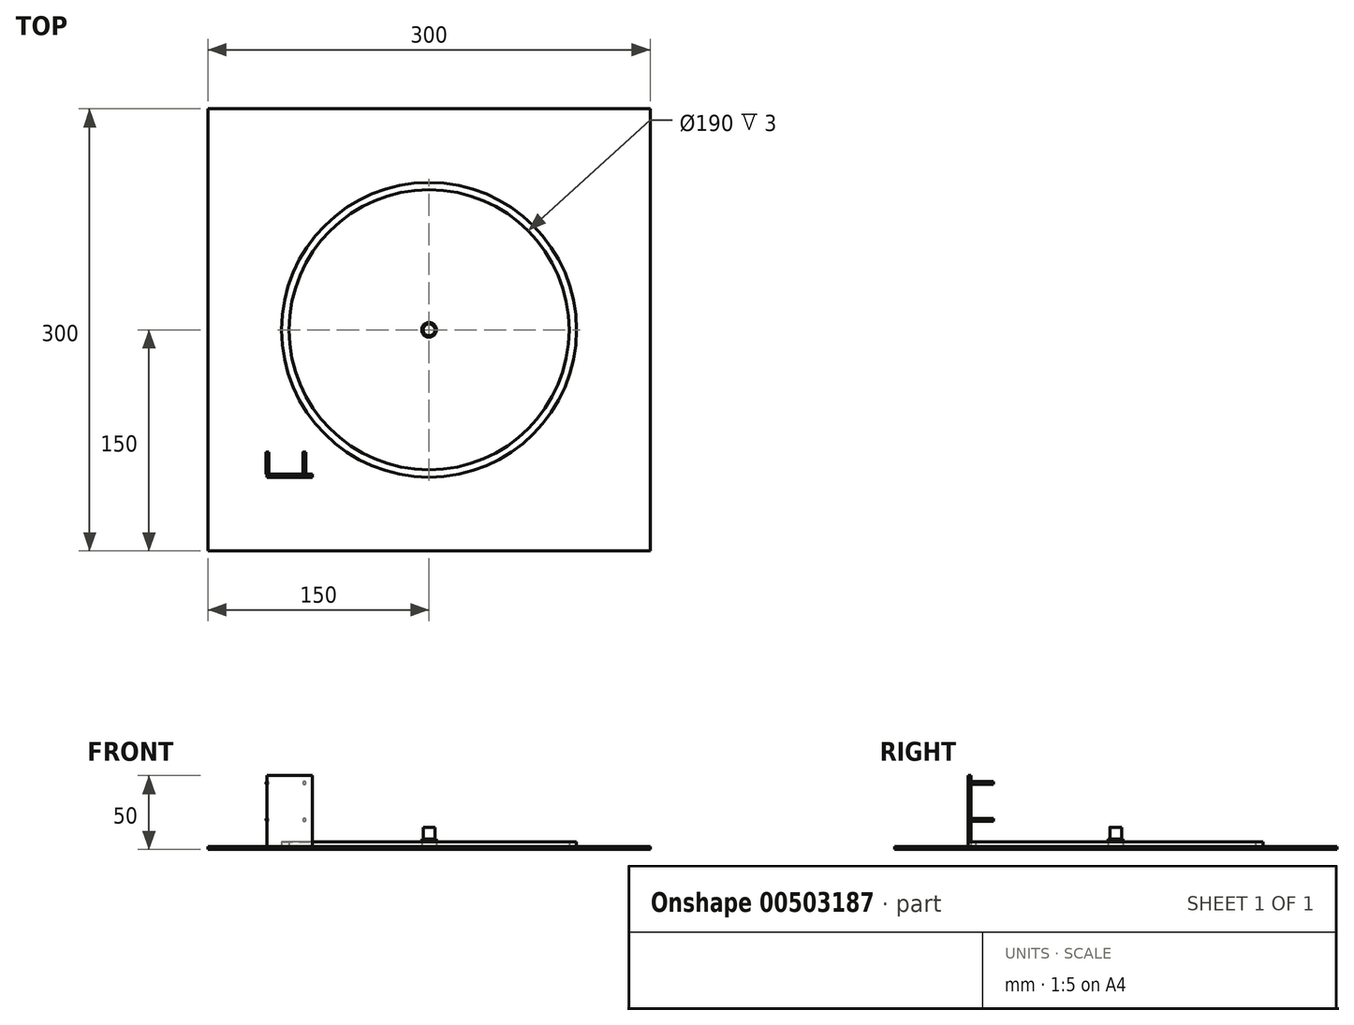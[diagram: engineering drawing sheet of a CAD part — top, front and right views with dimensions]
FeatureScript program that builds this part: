
annotation { "Feature Type Name" : "Feature", "Feature Type Description" : "" }
export const myFeature = defineFeature(function(context is Context, id is Id, definition is map)
    precondition{}
    {
        {
            var Q0;
            Q0=qCreatedBy(makeId("Top.planeOp"),FACE);
            var sketch = newSketch(context, id + "F0", { "sketchPlane" : qUnion([Q0])});
            skLineSegment(sketch, "E0.bottom", {"start": v(150, 150) * mm, "end": v(-150, 150) * mm});
            skLineSegment(sketch, "E0.top", {"start": v(150, -150) * mm, "end": v(-150, -150) * mm});
            skLineSegment(sketch, "E0.left", {"start": v(150, 150) * mm, "end": v(150, -150) * mm});
            skLineSegment(sketch, "E0.right", {"start": v(-150, 150) * mm, "end": v(-150, -150) * mm});
            skPoint(sketch, "E0.middle", {"position": v(0, 0) * mm});
            skCircle(sketch, "E1", {"center": v(0, 0) * mm, "radius": 5 * mm});
            skCircle(sketch, "E2", {"center": v(0, 0) * mm, "radius": 100 * mm});
            skCircle(sketch, "E3.0", {"center": v(0, 0) * mm, "radius": 95 * mm});
            skLineSegment(sketch, "E4.bottom", {"start": v(-110, -98) * mm, "end": v(-79.18, -98) * mm});
            skLineSegment(sketch, "E4.top", {"start": v(-110, -100) * mm, "end": v(-79.18, -100) * mm});
            skLineSegment(sketch, "E4.left", {"start": v(-110, -98) * mm, "end": v(-110, -100) * mm});
            skLineSegment(sketch, "E4.right", {"start": v(-79.18, -98) * mm, "end": v(-79.18, -100) * mm});
            skSolve(sketch);
        }
        {
            var Q0;
            Q0 = qSketchRegion(id + "F0", true);
            var Q1;
            Q1=makeQuery(id+"F0.imprint","IMPRINT",FACE,{"disambiguationData":[TD([[makeQuery(id+"F0.imprint","IMPRINT",EDGE,{"derivedFrom":sQuery(id+"F0.wireOp",EDGE,"E1")}),-1.0]])]});
            var Q2;
            Q2=makeQuery(id+"F0.imprint","IMPRINT",FACE,{"disambiguationData":[TD([[makeQuery(id+"F0.imprint","IMPRINT",EDGE,{"derivedFrom":sQuery(id+"F0.wireOp",EDGE,"E4.bottom")}),-1.0]])]});
            var Q3;
            Q3=makeQuery(id+"F0.imprint","IMPRINT",FACE,{"disambiguationData":[TD([[makeQuery(id+"F0.imprint","IMPRINT",EDGE,{"derivedFrom":sQuery(id+"F0.wireOp",EDGE,"E2")}),1.0]])]});
            extrude(context, id + "F1", {"entities" : qUnion([Q0, Q1, Q2, Q3]), "depth" : 2 * mm});
        }
        {
            var Q0;
            Q0=makeQuery(id+"F0.imprint","IMPRINT",FACE,{"disambiguationData":[TD([[makeQuery(id+"F0.imprint","IMPRINT",EDGE,{"derivedFrom":sQuery(id+"F0.wireOp",EDGE,"E1")}),1.0]])]});
            extrude(context, id + "F2", {"entities" : qUnion([Q0]), "operationType" : NewBodyOperationType.ADD, "depth" : 15 * mm});
        }
        {
            var Q0;
            Q0=makeQuery(id+"F0.imprint","IMPRINT",FACE,{"disambiguationData":[TD([[makeQuery(id+"F0.imprint","IMPRINT",EDGE,{"derivedFrom":sQuery(id+"F0.wireOp",EDGE,"E2")}),1.0]])]});
            var Q1;
            Q1=sQuery(id+"F0.wireOp",EDGE,"E2");
            var Q2;
            Q2=sQuery(id+"F0.wireOp",EDGE,"E3.0");
            extrude(context, id + "F3", {"entities" : qUnion([Q0]), "operationType" : NewBodyOperationType.ADD, "surfaceEntities" : qUnion([Q1, Q2]), "depth" : 5 * mm});
        }
        {
            var Q0;
            Q0=makeQuery(id+"F0.imprint","IMPRINT",FACE,{"disambiguationData":[TD([[makeQuery(id+"F0.imprint","IMPRINT",EDGE,{"derivedFrom":sQuery(id+"F0.wireOp",EDGE,"E4.bottom")}),-1.0]])]});
            extrude(context, id + "F4", {"entities" : qUnion([Q0]), "operationType" : NewBodyOperationType.ADD, "depth" : 50 * mm});
        }
        {
            var Q0;
            Q0=makeQuery(id+"F4.opExtrude","SWEPT_FACE",FACE,{"disambiguationData":[OSD([sQuery(id+"F0.wireOp",EDGE,"E4.bottom")])]});
            var sketch = newSketch(context, id + "F5", { "sketchPlane" : qUnion([Q0])});
            skLineSegment(sketch, "E5.bottom", {"start": v(84.58, 45) * mm, "end": v(109.58, 45) * mm, "construction": true});
            skLineSegment(sketch, "E5.top", {"start": v(84.58, 20) * mm, "end": v(109.58, 20) * mm, "construction": true});
            skLineSegment(sketch, "E5.left", {"start": v(84.58, 45) * mm, "end": v(84.58, 20) * mm, "construction": true});
            skLineSegment(sketch, "E5.right", {"start": v(109.58, 45) * mm, "end": v(109.58, 20) * mm, "construction": true});
            skCircle(sketch, "E6", {"center": v(84.58, 45) * mm, "radius": 1 * mm});
            skCircle(sketch, "E7", {"center": v(109.58, 45) * mm, "radius": 1 * mm});
            skCircle(sketch, "E8", {"center": v(109.58, 20) * mm, "radius": 1 * mm});
            skCircle(sketch, "E9", {"center": v(84.58, 20) * mm, "radius": 1 * mm});
            skSolve(sketch);
        }
        {
            var Q0;
            Q0=makeQuery(id+"F5.imprint","IMPRINT",FACE,{"disambiguationData":[TD([[makeQuery(id+"F5.imprint","IMPRINT",EDGE,{"derivedFrom":sQuery(id+"F5.wireOp",EDGE,"E6")}),1.0]])]});
            var Q1;
            Q1=makeQuery(id+"F5.imprint","IMPRINT",FACE,{"disambiguationData":[TD([[makeQuery(id+"F5.imprint","IMPRINT",EDGE,{"derivedFrom":sQuery(id+"F5.wireOp",EDGE,"E7")}),1.0]])]});
            var Q2;
            Q2=makeQuery(id+"F5.imprint","IMPRINT",FACE,{"disambiguationData":[TD([[makeQuery(id+"F5.imprint","IMPRINT",EDGE,{"derivedFrom":sQuery(id+"F5.wireOp",EDGE,"E8")}),1.0]])]});
            var Q3;
            Q3=makeQuery(id+"F5.imprint","IMPRINT",FACE,{"disambiguationData":[TD([[makeQuery(id+"F5.imprint","IMPRINT",EDGE,{"derivedFrom":sQuery(id+"F5.wireOp",EDGE,"E9")}),1.0]])]});
            extrude(context, id + "F6", {"entities" : qUnion([Q0, Q1, Q2, Q3]), "operationType" : NewBodyOperationType.ADD, "depth" : 15 * mm});
        }
        {
            var Q0;
            Q0=makeQuery(id+"F2.opExtrude","CAP_FACE",FACE,{"disambiguationData":[OSD([sQuery(id+"F0.wireOp",EDGE,"E1")])],"isStart":false});
            var sketch = newSketch(context, id + "F7", { "sketchPlane" : qUnion([Q0])});
            skCircle(sketch, "E10", {"center": v(0, 0) * mm, "radius": 4 * mm});
            skCircle(sketch, "E11", {"center": v(0, 0) * mm, "radius": 7.66 * mm});
            skSolve(sketch);
        }
        {
            var Q0;
            Q0=makeQuery(id+"F7.imprint","IMPRINT",FACE,{"disambiguationData":[TD([[makeQuery(id+"F7.imprint","IMPRINT",EDGE,{"derivedFrom":sQuery(id+"F7.wireOp",EDGE,"E10")}),-1.0]])]});
            extrude(context, id + "F8", {"entities" : qUnion([Q0]), "operationType" : NewBodyOperationType.REMOVE, "oppositeDirection" : true, "depth" : 8 * mm});
        }
    });
